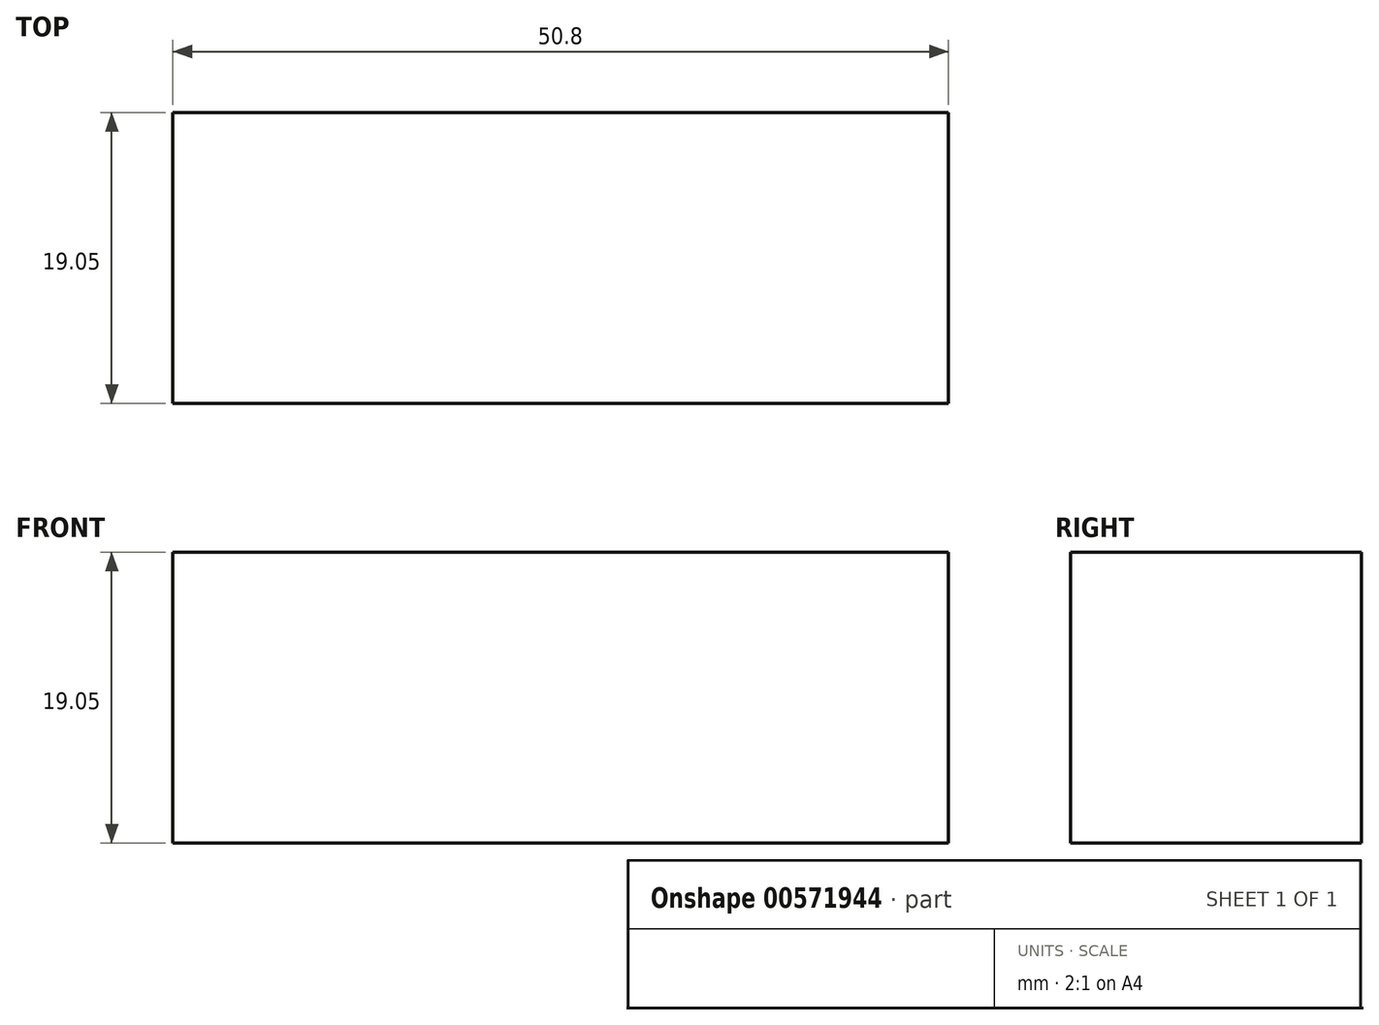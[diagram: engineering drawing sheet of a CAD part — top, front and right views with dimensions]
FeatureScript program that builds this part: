
annotation { "Feature Type Name" : "Feature", "Feature Type Description" : "" }
export const myFeature = defineFeature(function(context is Context, id is Id, definition is map)
    precondition{}
    {
        {
            var Q0;
            Q0=qCreatedBy(makeId("Front.planeOp"),FACE);
            var sketch = newSketch(context, id + "F0", { "sketchPlane" : qUnion([Q0])});
            skLineSegment(sketch, "E0.bottom", {"start": v(0, 0) * mm, "end": v(-50.8, 0) * mm});
            skLineSegment(sketch, "E0.top", {"start": v(0, -19.05) * mm, "end": v(-50.8, -19.05) * mm});
            skLineSegment(sketch, "E0.left", {"start": v(0, 0) * mm, "end": v(0, -19.05) * mm});
            skLineSegment(sketch, "E0.right", {"start": v(-50.8, 0) * mm, "end": v(-50.8, -19.05) * mm});
            skSolve(sketch);
        }
        {
            var Q0;
            Q0 = qSketchRegion(id + "F0", true);
            extrude(context, id + "F1", {"entities" : qUnion([Q0]), "depth" : 19.05 * mm, "offsetDistance" : 25.4 * mm});
        }
    });
